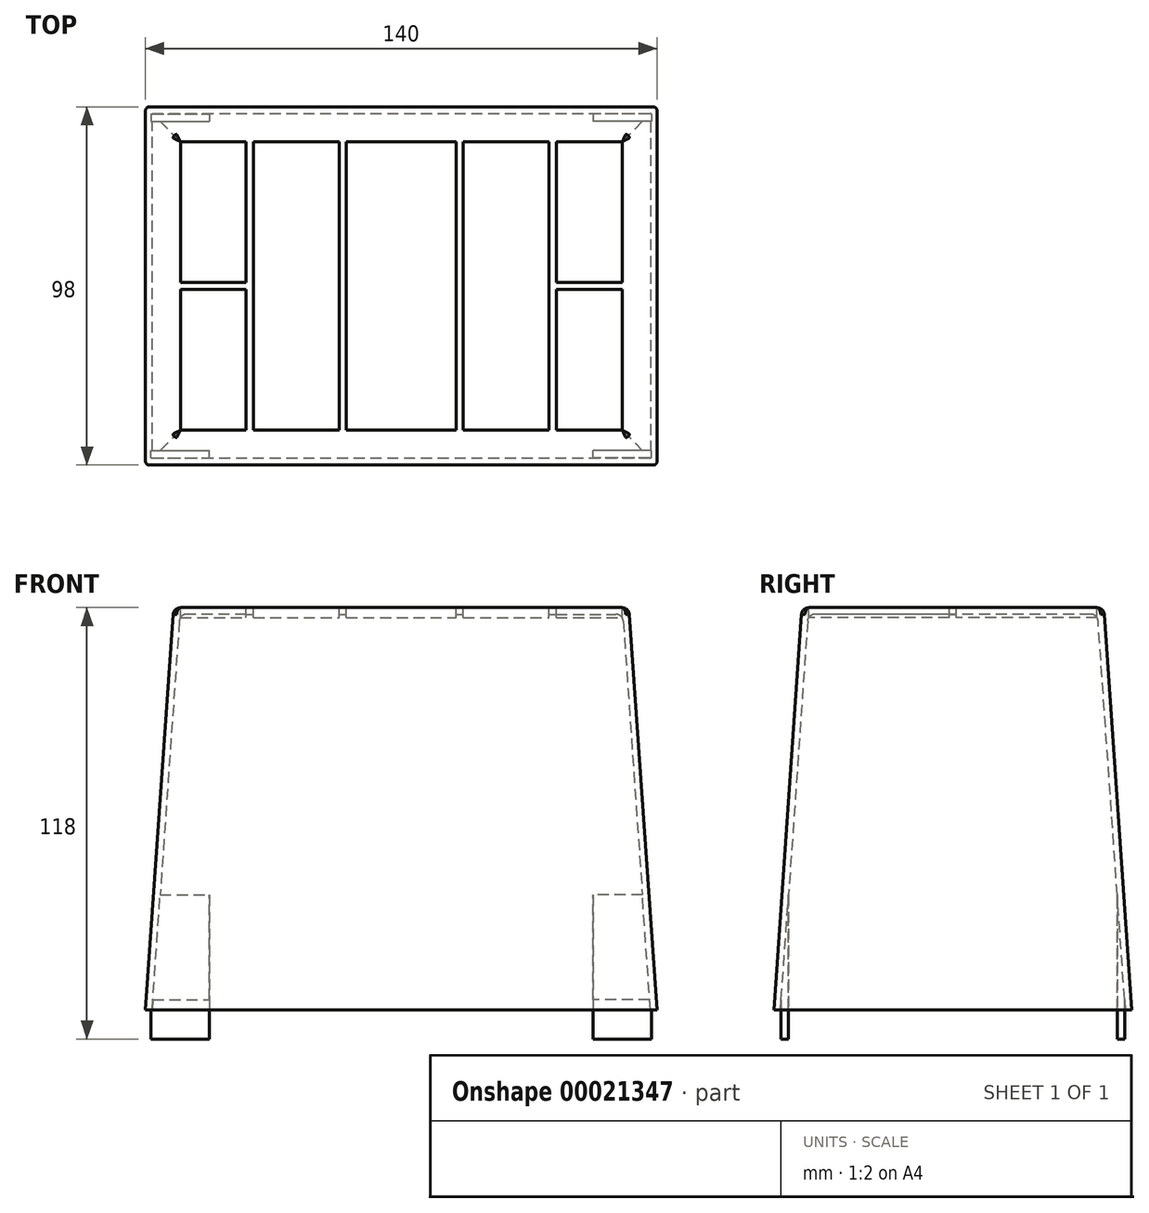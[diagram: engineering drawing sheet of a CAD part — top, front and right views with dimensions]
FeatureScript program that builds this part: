
annotation { "Feature Type Name" : "Feature", "Feature Type Description" : "" }
export const myFeature = defineFeature(function(context is Context, id is Id, definition is map)
    precondition{}
    {
        {
            var Q0;
            Q0=qCreatedBy(makeId("Top.planeOp"),FACE);
            var sketch = newSketch(context, id + "F0", { "sketchPlane" : qUnion([Q0])});
            skLineSegment(sketch, "E0.bottom", {"start": v(70, -49) * mm, "end": v(-70, -49) * mm});
            skLineSegment(sketch, "E0.top", {"start": v(70, 49) * mm, "end": v(-70, 49) * mm});
            skLineSegment(sketch, "E0.left", {"start": v(70, -49) * mm, "end": v(70, 49) * mm});
            skLineSegment(sketch, "E0.right", {"start": v(-70, -49) * mm, "end": v(-70, 49) * mm});
            skLineSegment(sketch, "E1", {"start": v(-70, -49) * mm, "end": v(70, 49) * mm});
            skPoint(sketch, "E2", {"position": v(0, 0) * mm});
            skSolve(sketch);
        }
        {
            var Q0;
            Q0=makeQuery(id+"F0.imprint","IMPRINT",FACE,{"disambiguationData":[TD([[makeQuery(id+"F0.imprint","IMPRINT",EDGE,{"derivedFrom":sQuery(id+"F0.wireOp",EDGE,"E0.top")}),1.0]])]});
            var Q1;
            Q1=makeQuery(id+"F0.imprint","IMPRINT",FACE,{"disambiguationData":[TD([[makeQuery(id+"F0.imprint","IMPRINT",EDGE,{"derivedFrom":sQuery(id+"F0.wireOp",EDGE,"E0.bottom")}),-1.0]])]});
            extrude(context, id + "F1", {"entities" : qUnion([Q0, Q1]), "depth" : 110 * mm, "hasDraft" : true, "draftAngle" : 4 * degree, "draftPullDirection" : true});
        }
        {
            var Q0;
            Q0=makeQuery(id+"F1.opExtrude","SWEPT_EDGE",EDGE,{"disambiguationData":[OSD([sQuery(id+"F0.wireOp",EDGE,"E0.bottom"),sQuery(id+"F0.wireOp",EDGE,"E0.right"),sQuery(id+"F0.wireOp",EDGE,"E1")])]});
            var Q1;
            Q1=makeQuery(id+"F1.opExtrude","SWEPT_EDGE",EDGE,{"disambiguationData":[OSD([sQuery(id+"F0.wireOp",EDGE,"E0.bottom"),sQuery(id+"F0.wireOp",EDGE,"E0.left")])]});
            var Q2;
            Q2=makeQuery(id+"F1.opExtrude","SWEPT_EDGE",EDGE,{"disambiguationData":[OSD([sQuery(id+"F0.wireOp",EDGE,"E0.top"),sQuery(id+"F0.wireOp",EDGE,"E0.left"),sQuery(id+"F0.wireOp",EDGE,"E1")])]});
            var Q3;
            Q3=makeQuery(id+"F1.opExtrude","SWEPT_EDGE",EDGE,{"disambiguationData":[OSD([sQuery(id+"F0.wireOp",EDGE,"E0.top"),sQuery(id+"F0.wireOp",EDGE,"E0.right")])]});
            fillet(context, id + "F2", {"entities" : qUnion([Q0, Q1, Q2, Q3]), "radius" : 1 * mm, "tangentPropagation" : true, "allowEdgeOverflow" : false});
        }
        {
            var Q0;
            Q0=makeQuery(id+"F1.opExtrude","CAP_FACE",FACE,{"disambiguationData":[OSD([sQuery(id+"F0.wireOp",EDGE,"E0.bottom"),sQuery(id+"F0.wireOp",EDGE,"E0.top"),sQuery(id+"F0.wireOp",EDGE,"E0.left"),sQuery(id+"F0.wireOp",EDGE,"E0.right")])],"isStart":true});
            shell(context, id + "F3", {"entities" : qUnion([Q0]), "thickness" : 1.8 * mm});
        }
        {
            var Q0;
            Q0=makeQuery(id+"F3.opShell","OFFSET_FACE",FACE,{"disambiguationData":[OSD([sQuery(id+"F0.wireOp",EDGE,"E0.bottom"),sQuery(id+"F0.wireOp",EDGE,"E0.top"),sQuery(id+"F0.wireOp",EDGE,"E0.left"),sQuery(id+"F0.wireOp",EDGE,"E0.right")])]});
            var Q1;
            Q1=makeQuery(id+"F1.opExtrude","CAP_FACE",FACE,{"disambiguationData":[OSD([sQuery(id+"F0.wireOp",EDGE,"E0.bottom"),sQuery(id+"F0.wireOp",EDGE,"E0.top"),sQuery(id+"F0.wireOp",EDGE,"E0.left"),sQuery(id+"F0.wireOp",EDGE,"E0.right")])],"isStart":false});
            fillet(context, id + "F4", {"entities" : qUnion([Q0, Q1]), "radius" : 2 * mm, "tangentPropagation" : true, "allowEdgeOverflow" : false});
        }
        {
            var Q0;
            Q0=makeQuery(id+"F1.opExtrude","CAP_FACE",FACE,{"disambiguationData":[OSD([sQuery(id+"F0.wireOp",EDGE,"E0.bottom"),sQuery(id+"F0.wireOp",EDGE,"E0.top"),sQuery(id+"F0.wireOp",EDGE,"E0.left"),sQuery(id+"F0.wireOp",EDGE,"E0.right")])],"isStart":false});
            var sketch = newSketch(context, id + "F5", { "sketchPlane" : qUnion([Q0])});
            skLineSegment(sketch, "E3.0", {"start": v(61.44, -41.44) * mm, "end": v(-61.44, -41.44) * mm});
            skEllipticalArc(sketch, "E4.0", {});
            skLineSegment(sketch, "E5.0", {"start": v(-62.44, -40.44) * mm, "end": v(-62.44, 40.44) * mm});
            skEllipticalArc(sketch, "E6.0", {});
            skLineSegment(sketch, "E7.0", {"start": v(-61.44, 41.44) * mm, "end": v(61.44, 41.44) * mm});
            skEllipticalArc(sketch, "E8.0", {});
            skLineSegment(sketch, "E9.0", {"start": v(62.44, 40.44) * mm, "end": v(62.44, -40.44) * mm});
            skEllipticalArc(sketch, "E10.0", {});
            skLineSegment(sketch, "E11.bottom", {"start": v(-42.44, 41.44) * mm, "end": v(-40.44, 41.44) * mm});
            skLineSegment(sketch, "E11.top", {"start": v(-42.44, -41.44) * mm, "end": v(-40.44, -41.44) * mm});
            skLineSegment(sketch, "E11.left", {"start": v(-42.44, 41.44) * mm, "end": v(-42.44, -41.44) * mm});
            skLineSegment(sketch, "E11.right", {"start": v(-40.44, 41.44) * mm, "end": v(-40.44, -41.44) * mm});
            skLineSegment(sketch, "E12.bottom", {"start": v(-17, 41.44) * mm, "end": v(-15, 41.44) * mm});
            skLineSegment(sketch, "E12.top", {"start": v(-17, -41.44) * mm, "end": v(-15, -41.44) * mm});
            skLineSegment(sketch, "E12.left", {"start": v(-17, 41.44) * mm, "end": v(-17, -41.44) * mm});
            skLineSegment(sketch, "E12.right", {"start": v(-15, 41.44) * mm, "end": v(-15, -41.44) * mm});
            skLineSegment(sketch, "E13.bottom", {"start": v(15, 41.44) * mm, "end": v(17, 41.44) * mm});
            skLineSegment(sketch, "E13.top", {"start": v(15, -41.44) * mm, "end": v(17, -41.44) * mm});
            skLineSegment(sketch, "E13.left", {"start": v(15, 41.44) * mm, "end": v(15, -41.44) * mm});
            skLineSegment(sketch, "E13.right", {"start": v(17, 41.44) * mm, "end": v(17, -41.44) * mm});
            skLineSegment(sketch, "E14.bottom", {"start": v(40.44, 41.44) * mm, "end": v(42.44, 41.44) * mm});
            skLineSegment(sketch, "E14.top", {"start": v(40.44, -41.44) * mm, "end": v(42.44, -41.44) * mm});
            skLineSegment(sketch, "E14.left", {"start": v(40.44, 41.44) * mm, "end": v(40.44, -41.44) * mm});
            skLineSegment(sketch, "E14.right", {"start": v(42.44, 41.44) * mm, "end": v(42.44, -41.44) * mm});
            skLineSegment(sketch, "E15.bottom", {"start": v(42.44, 1) * mm, "end": v(62.44, 1) * mm});
            skLineSegment(sketch, "E15.top", {"start": v(42.44, -1) * mm, "end": v(62.44, -1) * mm});
            skLineSegment(sketch, "E15.left", {"start": v(42.44, 1) * mm, "end": v(42.44, -1) * mm});
            skLineSegment(sketch, "E15.right", {"start": v(62.44, 1) * mm, "end": v(62.44, -1) * mm});
            skLineSegment(sketch, "E16.bottom", {"start": v(-42.44, 1) * mm, "end": v(-62.44, 1) * mm});
            skLineSegment(sketch, "E16.top", {"start": v(-42.44, -1) * mm, "end": v(-62.44, -1) * mm});
            skLineSegment(sketch, "E16.left", {"start": v(-42.44, 1) * mm, "end": v(-42.44, -1) * mm});
            skLineSegment(sketch, "E16.right", {"start": v(-62.44, 1) * mm, "end": v(-62.44, -1) * mm});
            skLineSegment(sketch, "E17", {"start": v(-15, 0) * mm, "end": v(0, 0) * mm, "construction": true});
            skLineSegment(sketch, "E18", {"start": v(0, 0) * mm, "end": v(15, 0) * mm, "construction": true});
            skPoint(sketch, "E19", {"position": v(-42.44, 0) * mm});
            skPoint(sketch, "E20", {"position": v(42.44, 0) * mm});
            const initialGuessF5  = {"E4.0": [-0.05073817372554934, -0.016738173725549366, -0.7071067811865563, 0.7071067811865387, 0.001, 0.0009808148484639894, 0.7950833450659078, 2.346509308523878], "E6.0": [-0.05073817372554933, 0.016738173725549317, 0.7071067811865551, 0.70710678118654, 0.001, 0.0009808148484639885, 0.7950833450659279, 2.3465093085238866], "E8.0": [0.05073817372554934, 0.01673817372554933, 0.7071067811865476, -0.7071067811865476, 0.001, 0.000980814848463989, 0.7950833450659242, 2.34650930852389], "E10.0": [0.05073817372554934, -0.016738173725549355, -0.7071067811865476, -0.7071067811865476, 0.001, 0.000980814848463989, 0.7950833450659099, 2.3465093085238764]};
            skSetInitialGuess(sketch, initialGuessF5);
            skSolve(sketch);
        }
        {
            var Q0;
            {var subQ5=sQuery(id+"F5.wireOp",EDGE,"E15.bottom");var subQ9=sQuery(id+"F5.wireOp",EDGE,"E14.right");var subQ11=makeQuery(id+"F5.imprint","INTERSECT",VERTEX,{"derivedFrom":[subQ9,subQ5,sQuery(id+"F5.wireOp",EDGE,"E15.left")]});Q0=makeQuery(id+"F5.imprint","IMPRINT",FACE,{"disambiguationData":[TD([[makeQuery(id+"F5.imprint","IMPRINT",EDGE,{"disambiguationData":[TD([[subQ11,1.0]])],"derivedFrom":subQ9}),1.0]])]});}
            var Q1;
            {var subQ5=sQuery(id+"F5.wireOp",EDGE,"E15.top");var subQ9=sQuery(id+"F5.wireOp",EDGE,"E14.right");var subQ11=makeQuery(id+"F5.imprint","INTERSECT",VERTEX,{"derivedFrom":[subQ9,subQ5,sQuery(id+"F5.wireOp",EDGE,"E15.left")]});Q1=makeQuery(id+"F5.imprint","IMPRINT",FACE,{"disambiguationData":[TD([[makeQuery(id+"F5.imprint","IMPRINT",EDGE,{"disambiguationData":[TD([[subQ11,-1.0]])],"derivedFrom":subQ9}),1.0]])]});}
            var Q2;
            {var subQ0=sQuery(id+"F0.wireOp",EDGE,"E0.top");var subQ1=sQuery(id+"F0.wireOp",EDGE,"E0.bottom");var subQ2=makeQuery(id+"F1.opExtrude","CAP_FACE",FACE,{"disambiguationData":[OSD([subQ1,subQ0,sQuery(id+"F0.wireOp",EDGE,"E0.left"),sQuery(id+"F0.wireOp",EDGE,"E0.right")])],"isStart":false});var subQ3=makeQuery(id+"F4.opFillet","BLEND_EDGE",EDGE,{"blendedFrom":[makeQuery(id+"F1.opExtrude","CAP_EDGE",EDGE,{"disambiguationData":[OSD([subQ0])],"isStart":false}),subQ2],"blendedInto":[subQ2]});var subQ6=sQuery(id+"F5.wireOp",EDGE,"E13.right");var subQ7=makeQuery(id+"F5.imprint","INTERSECT",VERTEX,{"derivedFrom":[subQ3,subQ6]});Q2=makeQuery(id+"F5.imprint","IMPRINT",FACE,{"disambiguationData":[TD([[makeQuery(id+"F5.imprint","IMPRINT",EDGE,{"disambiguationData":[TD([[subQ7,-1.0]])],"derivedFrom":subQ6}),1.0]])]});}
            var Q3;
            {var subQ0=sQuery(id+"F0.wireOp",EDGE,"E0.top");var subQ1=sQuery(id+"F0.wireOp",EDGE,"E0.bottom");var subQ2=makeQuery(id+"F1.opExtrude","CAP_FACE",FACE,{"disambiguationData":[OSD([subQ1,subQ0,sQuery(id+"F0.wireOp",EDGE,"E0.left"),sQuery(id+"F0.wireOp",EDGE,"E0.right")])],"isStart":false});var subQ3=makeQuery(id+"F4.opFillet","BLEND_EDGE",EDGE,{"blendedFrom":[makeQuery(id+"F1.opExtrude","CAP_EDGE",EDGE,{"disambiguationData":[OSD([subQ0])],"isStart":false}),subQ2],"blendedInto":[subQ2]});var subQ6=sQuery(id+"F5.wireOp",EDGE,"E12.right");var subQ7=makeQuery(id+"F5.imprint","INTERSECT",VERTEX,{"derivedFrom":[subQ3,subQ6]});Q3=makeQuery(id+"F5.imprint","IMPRINT",FACE,{"disambiguationData":[TD([[makeQuery(id+"F5.imprint","IMPRINT",EDGE,{"disambiguationData":[TD([[subQ7,-1.0]])],"derivedFrom":subQ6}),1.0]])]});}
            var Q4;
            {var subQ0=sQuery(id+"F0.wireOp",EDGE,"E0.top");var subQ1=sQuery(id+"F0.wireOp",EDGE,"E0.bottom");var subQ2=makeQuery(id+"F1.opExtrude","CAP_FACE",FACE,{"disambiguationData":[OSD([subQ1,subQ0,sQuery(id+"F0.wireOp",EDGE,"E0.left"),sQuery(id+"F0.wireOp",EDGE,"E0.right")])],"isStart":false});var subQ3=makeQuery(id+"F4.opFillet","BLEND_EDGE",EDGE,{"blendedFrom":[makeQuery(id+"F1.opExtrude","CAP_EDGE",EDGE,{"disambiguationData":[OSD([subQ0])],"isStart":false}),subQ2],"blendedInto":[subQ2]});var subQ6=sQuery(id+"F5.wireOp",EDGE,"E11.right");var subQ7=makeQuery(id+"F5.imprint","INTERSECT",VERTEX,{"derivedFrom":[subQ3,subQ6]});Q4=makeQuery(id+"F5.imprint","IMPRINT",FACE,{"disambiguationData":[TD([[makeQuery(id+"F5.imprint","IMPRINT",EDGE,{"disambiguationData":[TD([[subQ7,-1.0]])],"derivedFrom":subQ6}),1.0]])]});}
            var Q5;
            {var subQ5=sQuery(id+"F5.wireOp",EDGE,"E16.bottom");var subQ9=sQuery(id+"F5.wireOp",EDGE,"E11.left");var subQ11=makeQuery(id+"F5.imprint","INTERSECT",VERTEX,{"derivedFrom":[subQ9,subQ5,sQuery(id+"F5.wireOp",EDGE,"E16.left")]});Q5=makeQuery(id+"F5.imprint","IMPRINT",FACE,{"disambiguationData":[TD([[makeQuery(id+"F5.imprint","IMPRINT",EDGE,{"disambiguationData":[TD([[subQ11,1.0]])],"derivedFrom":subQ9}),-1.0]])]});}
            var Q6;
            {var subQ5=sQuery(id+"F5.wireOp",EDGE,"E16.top");var subQ9=sQuery(id+"F5.wireOp",EDGE,"E11.left");var subQ11=makeQuery(id+"F5.imprint","INTERSECT",VERTEX,{"derivedFrom":[subQ9,subQ5,sQuery(id+"F5.wireOp",EDGE,"E16.left")]});Q6=makeQuery(id+"F5.imprint","IMPRINT",FACE,{"disambiguationData":[TD([[makeQuery(id+"F5.imprint","IMPRINT",EDGE,{"disambiguationData":[TD([[subQ11,-1.0]])],"derivedFrom":subQ9}),-1.0]])]});}
            extrude(context, id + "F6", {"entities" : qUnion([Q0, Q1, Q2, Q3, Q4, Q5, Q6]), "operationType" : NewBodyOperationType.REMOVE, "oppositeDirection" : true, "depth" : 3 * mm});
        }
        {
            var Q0;
            Q0=makeQuery(id+"F1.opExtrude","CAP_FACE",FACE,{"disambiguationData":[OSD([sQuery(id+"F0.wireOp",EDGE,"E0.bottom"),sQuery(id+"F0.wireOp",EDGE,"E0.top"),sQuery(id+"F0.wireOp",EDGE,"E0.left"),sQuery(id+"F0.wireOp",EDGE,"E0.right")])],"isStart":true});
            cPlane(context, id + "F7", {"entities" : qUnion([Q0]), "cplaneType" : CPlaneType.OFFSET, "offset" : 8 * mm, "width" : 150 * mm, "height" : 150 * mm});
        }
        {
            var Q0;
            Q0=qCreatedBy(id+"F7.planeOp",FACE);
            var sketch = newSketch(context, id + "F8", { "sketchPlane" : qUnion([Q0])});
            skLineSegment(sketch, "E21.bottom", {"start": v(-68.5, 47) * mm, "end": v(68.5, 47) * mm, "construction": true});
            skLineSegment(sketch, "E21.top", {"start": v(-68.5, -47) * mm, "end": v(68.5, -47) * mm, "construction": true});
            skLineSegment(sketch, "E21.left", {"start": v(-68.5, 47) * mm, "end": v(-68.5, -47) * mm, "construction": true});
            skLineSegment(sketch, "E21.right", {"start": v(68.5, 47) * mm, "end": v(68.5, -47) * mm, "construction": true});
            skLineSegment(sketch, "E22", {"start": v(-68.5, 47) * mm, "end": v(68.5, -47) * mm, "construction": true});
            skLineSegment(sketch, "E23", {"start": v(68.5, 47) * mm, "end": v(-68.5, -47) * mm, "construction": true});
            skPoint(sketch, "E24", {"position": v(0, 0) * mm});
            skLineSegment(sketch, "E25.bottom", {"start": v(-68.5, 47) * mm, "end": v(-52.5, 47) * mm});
            skLineSegment(sketch, "E25.top", {"start": v(-68.5, 45) * mm, "end": v(-52.5, 45) * mm});
            skLineSegment(sketch, "E25.left", {"start": v(-68.5, 47) * mm, "end": v(-68.5, 45) * mm});
            skLineSegment(sketch, "E25.right", {"start": v(-52.5, 47) * mm, "end": v(-52.5, 45) * mm});
            skLineSegment(sketch, "E26.bottom", {"start": v(-68.5, -47) * mm, "end": v(-52.5, -47) * mm});
            skLineSegment(sketch, "E26.top", {"start": v(-68.5, -45) * mm, "end": v(-52.5, -45) * mm});
            skLineSegment(sketch, "E26.left", {"start": v(-68.5, -47) * mm, "end": v(-68.5, -45) * mm});
            skLineSegment(sketch, "E26.right", {"start": v(-52.5, -47) * mm, "end": v(-52.5, -45) * mm});
            skLineSegment(sketch, "E27.bottom", {"start": v(68.5, -47) * mm, "end": v(52.5, -47) * mm});
            skLineSegment(sketch, "E27.top", {"start": v(68.5, -45) * mm, "end": v(52.5, -45) * mm});
            skLineSegment(sketch, "E27.left", {"start": v(68.5, -47) * mm, "end": v(68.5, -45) * mm});
            skLineSegment(sketch, "E27.right", {"start": v(52.5, -47) * mm, "end": v(52.5, -45) * mm});
            skLineSegment(sketch, "E28.bottom", {"start": v(68.5, 47) * mm, "end": v(52.5, 47) * mm});
            skLineSegment(sketch, "E28.top", {"start": v(68.5, 45) * mm, "end": v(52.5, 45) * mm});
            skLineSegment(sketch, "E28.left", {"start": v(68.5, 47) * mm, "end": v(68.5, 45) * mm});
            skLineSegment(sketch, "E28.right", {"start": v(52.5, 47) * mm, "end": v(52.5, 45) * mm});
            skSolve(sketch);
        }
        {
            var Q0;
            Q0=makeQuery(id+"F8.imprint","IMPRINT",FACE,{"disambiguationData":[TD([[makeQuery(id+"F8.imprint","IMPRINT",EDGE,{"derivedFrom":sQuery(id+"F8.wireOp",EDGE,"E25.bottom")}),-1.0]])]});
            var Q1;
            Q1=makeQuery(id+"F8.imprint","IMPRINT",FACE,{"disambiguationData":[TD([[makeQuery(id+"F8.imprint","IMPRINT",EDGE,{"derivedFrom":sQuery(id+"F8.wireOp",EDGE,"E26.bottom")}),1.0]])]});
            var Q2;
            Q2=makeQuery(id+"F8.imprint","IMPRINT",FACE,{"disambiguationData":[TD([[makeQuery(id+"F8.imprint","IMPRINT",EDGE,{"derivedFrom":sQuery(id+"F8.wireOp",EDGE,"E27.bottom")}),-1.0]])]});
            var Q3;
            Q3=makeQuery(id+"F8.imprint","IMPRINT",FACE,{"disambiguationData":[TD([[makeQuery(id+"F8.imprint","IMPRINT",EDGE,{"derivedFrom":sQuery(id+"F8.wireOp",EDGE,"E28.bottom")}),1.0]])]});
            extrude(context, id + "F9", {"entities" : qUnion([Q0, Q1, Q2, Q3]), "operationType" : NewBodyOperationType.ADD, "endBound" : BoundingType.UP_TO_NEXT, "oppositeDirection" : true, "depth" : 25 * mm});
        }
    });
